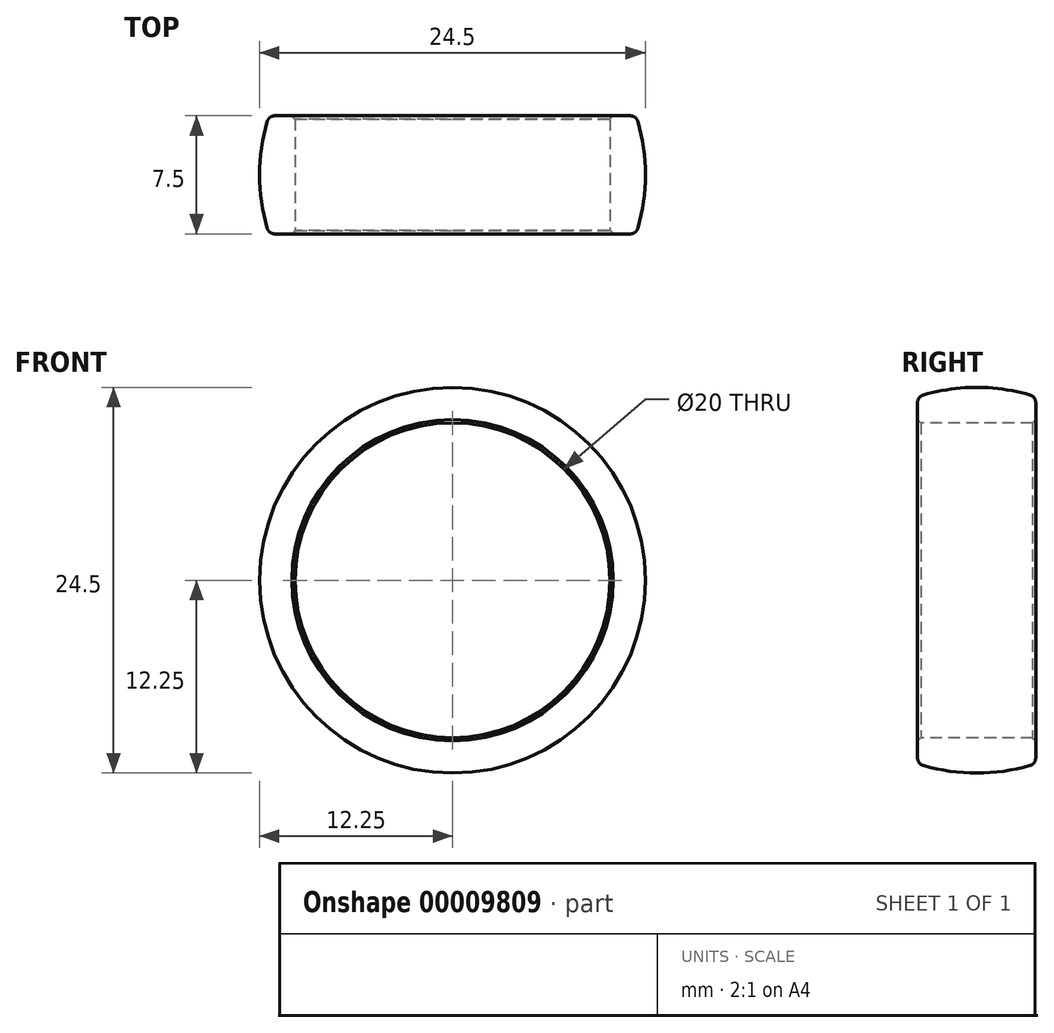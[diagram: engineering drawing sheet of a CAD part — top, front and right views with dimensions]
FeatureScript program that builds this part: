
annotation { "Feature Type Name" : "Feature", "Feature Type Description" : "" }
export const myFeature = defineFeature(function(context is Context, id is Id, definition is map)
    precondition{}
    {
        {
            var Q0;
            Q0=qCreatedBy(makeId("Right.planeOp"),FACE);
            var sketch = newSketch(context, id + "F0", { "sketchPlane" : qUnion([Q0])});
            skArc(sketch, "E0", {"start": v(3.75, 11.66) * mm, "mid": v(0, 12.25) * mm, "end": v(-3.75, 11.66) * mm});
            skLineSegment(sketch, "E1", {"start": v(-3.75, 11.66) * mm, "end": v(-3.75, 10) * mm});
            skLineSegment(sketch, "E2.0.MirrorCS", {"start": v(3.75, 11.66) * mm, "end": v(3.75, 10) * mm});
            skLineSegment(sketch, "E3", {"start": v(-3.75, 10) * mm, "end": v(3.75, 10) * mm});
            skSolve(sketch);
        }
        {
            var Q0;
            Q0=qCreatedBy(makeId("Top.planeOp"),FACE);
            var sketch = newSketch(context, id + "F1", { "sketchPlane" : qUnion([Q0])});
            skLineSegment(sketch, "E4", {"start": v(0, 0) * mm, "end": v(0, 13.57) * mm});
            skSolve(sketch);
        }
        {
            var Q0;
            Q0=makeQuery(id+"F0.imprint","IMPRINT",FACE,{"disambiguationData":[TD([[makeQuery(id+"F0.imprint","IMPRINT",EDGE,{"derivedFrom":sQuery(id+"F0.wireOp",EDGE,"E0")}),1.0]])]});
            var Q1;
            Q1=sQuery(id+"F1.wireOp",EDGE,"E4");
            revolve(context, id + "F2", {"entities" : qUnion([Q0]), "axis" : qUnion([Q1]), "revolveType" : RevolveType.FULL});
        }
        {
            var Q0;
            Q0=makeQuery(id+"F2.opRevolve","SWEPT_EDGE",EDGE,{"disambiguationData":[OSD([sQuery(id+"F0.wireOp",EDGE,"E1"),sQuery(id+"F0.wireOp",EDGE,"E3")])]});
            var Q1;
            Q1=makeQuery(id+"F2.opRevolve","SWEPT_EDGE",EDGE,{"disambiguationData":[OSD([sQuery(id+"F0.wireOp",EDGE,"E2.0.MirrorCS"),sQuery(id+"F0.wireOp",EDGE,"E3")])]});
            chamfer(context, id + "F3", {"entities" : qUnion([Q0, Q1]), "width" : 0.2 * mm, "tangentPropagation" : true});
        }
        {
            var Q0;
            Q0=makeQuery(id+"F2.opRevolve","SWEPT_EDGE",EDGE,{"disambiguationData":[OSD([sQuery(id+"F0.wireOp",EDGE,"E0"),sQuery(id+"F0.wireOp",EDGE,"E1")])]});
            var Q1;
            Q1=makeQuery(id+"F2.opRevolve","SWEPT_EDGE",EDGE,{"disambiguationData":[OSD([sQuery(id+"F0.wireOp",EDGE,"E0"),sQuery(id+"F0.wireOp",EDGE,"E2.0.MirrorCS")])]});
            fillet(context, id + "F4", {"entities" : qUnion([Q0, Q1]), "radius" : 0.5 * mm, "tangentPropagation" : true, "allowEdgeOverflow" : false});
        }
    });
